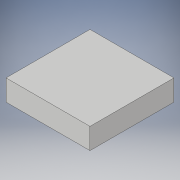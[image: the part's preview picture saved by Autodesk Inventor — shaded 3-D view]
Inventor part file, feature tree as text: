
AUTODESK INVENTOR PART (.ipt)
format: ipt  version: 2017 (Build 210142000, 142)  size: 86,528 bytes
history: native  units: in
note: dims shown in document units (in); Inventor stores cm internally (conversion verified against a paired STEP export)
features: extrude x1, sketch x1
ambient origin geometry x8: Origin, YZ Plane, XZ Plane, XY Plane, X Axis, Y Axis, Z Axis, Center Point
bodies: Solid1 (feature_tree)
feature tree (2):
  extrude  "Extrusion1"  Depth=0.5in
  sketch  "Sketch1"  dims[d0=2.0in d1=0.5in d2=2.0in d3=0.0in]
